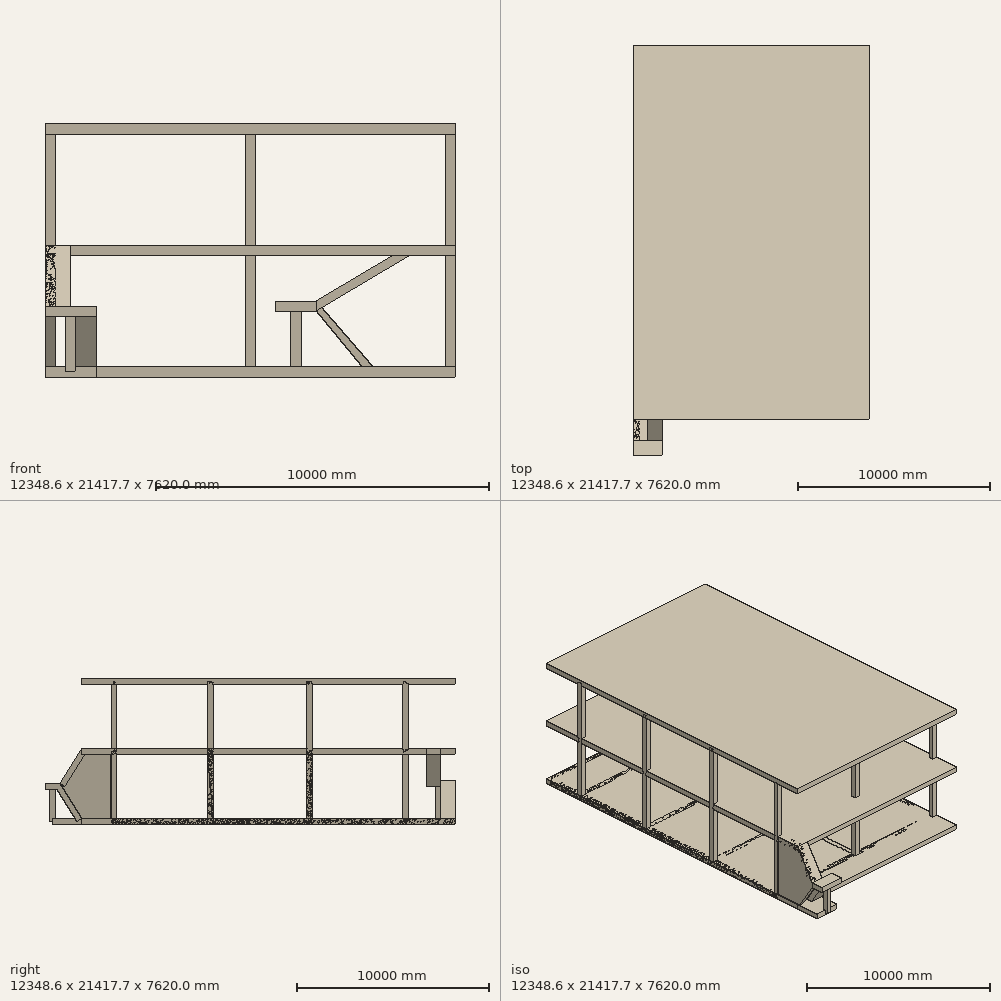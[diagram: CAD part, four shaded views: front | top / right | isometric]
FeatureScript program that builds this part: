
annotation { "Feature Type Name" : "Feature", "Feature Type Description" : "" }
export const myFeature = defineFeature(function(context is Context, id is Id, definition is map)
    precondition{}
    {
        {
            var Q0;
            Q0=qCreatedBy(makeId("Top.planeOp"),FACE);
            var sketch = newSketch(context, id + "F0", { "sketchPlane" : qUnion([Q0])});
            skLineSegment(sketch, "E0.bottom", {"start": v(6172.2, 8991.6) * mm, "end": v(-6172.2, 8991.6) * mm});
            skLineSegment(sketch, "E0.top", {"start": v(6172.2, -8991.6) * mm, "end": v(-6172.2, -8991.6) * mm});
            skLineSegment(sketch, "E0.left", {"start": v(6172.2, 8991.6) * mm, "end": v(6172.2, -8991.6) * mm});
            skLineSegment(sketch, "E0.right", {"start": v(-6172.2, 8991.6) * mm, "end": v(-6172.2, -8991.6) * mm});
            skPoint(sketch, "E0.middle", {"position": v(0, 0) * mm});
            skSolve(sketch);
        }
        {
            var Q0;
            Q0=qCreatedBy(makeId("Top.planeOp"),FACE);
            var sketch = newSketch(context, id + "F1", { "sketchPlane" : qUnion([Q0])});
            skLineSegment(sketch, "E1.bottom", {"start": v(-6172.2, -8991.6) * mm, "end": v(-5867.4, -8991.6) * mm});
            skLineSegment(sketch, "E1.top", {"start": v(-6172.2, -8686.8) * mm, "end": v(-5867.4, -8686.8) * mm});
            skLineSegment(sketch, "E1.left", {"start": v(-6172.2, -8991.6) * mm, "end": v(-6172.2, -8686.8) * mm});
            skLineSegment(sketch, "E1.right", {"start": v(-5867.4, -8991.6) * mm, "end": v(-5867.4, -8686.8) * mm});
            skSolve(sketch);
        }
        {
            var Q0;
            Q0 = qSketchRegion(id + "F1", true);
            extrude(context, id + "F2", {"entities" : qUnion([Q0]), "depth" : 7315.2 * mm, "offsetDistance" : 25.4 * mm});
        }
        {
            var Q0;
            Q0=qCreatedBy(makeId("Top.planeOp"),FACE);
            var sketch = newSketch(context, id + "F3", { "sketchPlane" : qUnion([Q0])});
            skLineSegment(sketch, "E2.bottom", {"start": v(6172.2, -8991.6) * mm, "end": v(5867.4, -8991.6) * mm});
            skLineSegment(sketch, "E2.top", {"start": v(6172.2, -8686.8) * mm, "end": v(5867.4, -8686.8) * mm});
            skLineSegment(sketch, "E2.left", {"start": v(6172.2, -8991.6) * mm, "end": v(6172.2, -8686.8) * mm});
            skLineSegment(sketch, "E2.right", {"start": v(5867.4, -8991.6) * mm, "end": v(5867.4, -8686.8) * mm});
            skSolve(sketch);
        }
        {
            var Q0;
            Q0 = qSketchRegion(id + "F3", true);
            extrude(context, id + "F4", {"entities" : qUnion([Q0]), "depth" : 7315.2 * mm, "offsetDistance" : 25.4 * mm});
        }
        {
            var Q0;
            Q0=qCreatedBy(makeId("Top.planeOp"),FACE);
            var sketch = newSketch(context, id + "F5", { "sketchPlane" : qUnion([Q0])});
            skLineSegment(sketch, "E3.bottom", {"start": v(6172.2, 6553.2) * mm, "end": v(5867.4, 6553.2) * mm});
            skLineSegment(sketch, "E3.top", {"start": v(6172.2, 6248.4) * mm, "end": v(5867.4, 6248.4) * mm});
            skLineSegment(sketch, "E3.left", {"start": v(6172.2, 6553.2) * mm, "end": v(6172.2, 6248.4) * mm});
            skLineSegment(sketch, "E3.right", {"start": v(5867.4, 6553.2) * mm, "end": v(5867.4, 6248.4) * mm});
            skSolve(sketch);
        }
        {
            var Q0;
            Q0 = qSketchRegion(id + "F5", true);
            extrude(context, id + "F6", {"entities" : qUnion([Q0]), "depth" : 7315.2 * mm, "offsetDistance" : 25.4 * mm});
        }
        {
            var Q0;
            Q0=qCreatedBy(makeId("Top.planeOp"),FACE);
            var sketch = newSketch(context, id + "F7", { "sketchPlane" : qUnion([Q0])});
            skLineSegment(sketch, "E4.bottom", {"start": v(-6172.2, 6248.4) * mm, "end": v(-5867.4, 6248.4) * mm});
            skLineSegment(sketch, "E4.top", {"start": v(-6172.2, 6553.2) * mm, "end": v(-5867.4, 6553.2) * mm});
            skLineSegment(sketch, "E4.left", {"start": v(-6172.2, 6248.4) * mm, "end": v(-6172.2, 6553.2) * mm});
            skLineSegment(sketch, "E4.right", {"start": v(-5867.4, 6248.4) * mm, "end": v(-5867.4, 6553.2) * mm});
            skSolve(sketch);
        }
        {
            var Q0;
            Q0 = qSketchRegion(id + "F7", true);
            extrude(context, id + "F8", {"entities" : qUnion([Q0]), "depth" : 7315.2 * mm, "offsetDistance" : 25.4 * mm});
        }
        {
            var Q0;
            Q0=qCreatedBy(makeId("Top.planeOp"),FACE);
            var sketch = newSketch(context, id + "F9", { "sketchPlane" : qUnion([Q0])});
            skLineSegment(sketch, "E5", {"start": v(0, 0) * mm, "end": v(0, 10809.08) * mm});
            skSolve(sketch);
        }
        {
            var Q0;
            Q0=qCreatedBy(makeId("Top.planeOp"),FACE);
            var sketch = newSketch(context, id + "F10", { "sketchPlane" : qUnion([Q0])});
            skLineSegment(sketch, "E6.bottom", {"start": v(152.4, 6248.4) * mm, "end": v(-152.4, 6248.4) * mm});
            skLineSegment(sketch, "E6.top", {"start": v(152.4, 6553.2) * mm, "end": v(-152.4, 6553.2) * mm});
            skLineSegment(sketch, "E6.left", {"start": v(152.4, 6248.4) * mm, "end": v(152.4, 6553.2) * mm});
            skLineSegment(sketch, "E6.right", {"start": v(-152.4, 6248.4) * mm, "end": v(-152.4, 6553.2) * mm});
            skPoint(sketch, "E6.middle", {"position": v(0, 6400.8) * mm});
            skSolve(sketch);
        }
        {
            var Q0;
            Q0=makeQuery(id+"F10.imprint","IMPRINT",FACE,{"disambiguationData":[TD([[makeQuery(id+"F10.imprint","IMPRINT",EDGE,{"derivedFrom":sQuery(id+"F10.wireOp",EDGE,"E6.bottom")}),-1.0]])]});
            extrude(context, id + "F11", {"entities" : qUnion([Q0]), "depth" : 7315.2 * mm, "offsetDistance" : 25.4 * mm});
        }
        {
            var Q0;
            Q0=qCreatedBy(makeId("Top.planeOp"),FACE);
            var sketch = newSketch(context, id + "F12", { "sketchPlane" : qUnion([Q0])});
            skLineSegment(sketch, "E7.bottom", {"start": v(152.4, -8991.6) * mm, "end": v(-152.4, -8991.6) * mm});
            skLineSegment(sketch, "E7.top", {"start": v(152.4, -8686.8) * mm, "end": v(-152.4, -8686.8) * mm});
            skLineSegment(sketch, "E7.left", {"start": v(152.4, -8991.6) * mm, "end": v(152.4, -8686.8) * mm});
            skLineSegment(sketch, "E7.right", {"start": v(-152.4, -8991.6) * mm, "end": v(-152.4, -8686.8) * mm});
            skPoint(sketch, "E7.middle", {"position": v(0, -8839.2) * mm});
            skSolve(sketch);
        }
        {
            var Q0;
            Q0 = qSketchRegion(id + "F12", true);
            extrude(context, id + "F13", {"entities" : qUnion([Q0]), "depth" : 7315.2 * mm, "offsetDistance" : 25.4 * mm});
        }
        {
            var Q0;
            Q0=qCreatedBy(makeId("Top.planeOp"),FACE);
            var sketch = newSketch(context, id + "F14", { "sketchPlane" : qUnion([Q0])});
            skLineSegment(sketch, "E8.bottom", {"start": v(152.4, -3962.4) * mm, "end": v(-152.4, -3962.4) * mm});
            skLineSegment(sketch, "E8.top", {"start": v(152.4, -3657.6) * mm, "end": v(-152.4, -3657.6) * mm});
            skLineSegment(sketch, "E8.left", {"start": v(152.4, -3962.4) * mm, "end": v(152.4, -3657.6) * mm});
            skLineSegment(sketch, "E8.right", {"start": v(-152.4, -3962.4) * mm, "end": v(-152.4, -3657.6) * mm});
            skPoint(sketch, "E8.middle", {"position": v(0, -3810) * mm});
            skSolve(sketch);
        }
        {
            var Q0;
            Q0=qCreatedBy(makeId("Top.planeOp"),FACE);
            var sketch = newSketch(context, id + "F15", { "sketchPlane" : qUnion([Q0])});
            skLineSegment(sketch, "E9.bottom", {"start": v(152.4, 1219.2) * mm, "end": v(-152.4, 1219.2) * mm});
            skLineSegment(sketch, "E9.top", {"start": v(152.4, 1524) * mm, "end": v(-152.4, 1524) * mm});
            skLineSegment(sketch, "E9.left", {"start": v(152.4, 1219.2) * mm, "end": v(152.4, 1524) * mm});
            skLineSegment(sketch, "E9.right", {"start": v(-152.4, 1219.2) * mm, "end": v(-152.4, 1524) * mm});
            skPoint(sketch, "E9.middle", {"position": v(0, 1371.6) * mm});
            skSolve(sketch);
        }
        {
            var Q0;
            Q0=makeQuery(id+"F14.imprint","IMPRINT",FACE,{"disambiguationData":[TD([[makeQuery(id+"F14.imprint","IMPRINT",EDGE,{"derivedFrom":sQuery(id+"F14.wireOp",EDGE,"E8.bottom")}),-1.0]])]});
            extrude(context, id + "F16", {"entities" : qUnion([Q0]), "depth" : 7315.2 * mm, "offsetDistance" : 25.4 * mm});
        }
        {
            var Q0;
            Q0 = qSketchRegion(id + "F15", true);
            extrude(context, id + "F17", {"entities" : qUnion([Q0]), "depth" : 7315.2 * mm, "offsetDistance" : 25.4 * mm});
        }
        {
            var Q0;
            Q0=qCreatedBy(makeId("Top.planeOp"),FACE);
            var sketch = newSketch(context, id + "F18", { "sketchPlane" : qUnion([Q0])});
            skLineSegment(sketch, "E10.bottom", {"start": v(6172.2, 1219.2) * mm, "end": v(5867.4, 1219.2) * mm});
            skLineSegment(sketch, "E10.top", {"start": v(6172.2, 1524) * mm, "end": v(5867.4, 1524) * mm});
            skLineSegment(sketch, "E10.left", {"start": v(6172.2, 1219.2) * mm, "end": v(6172.2, 1524) * mm});
            skLineSegment(sketch, "E10.right", {"start": v(5867.4, 1219.2) * mm, "end": v(5867.4, 1524) * mm});
            skPoint(sketch, "E10.middle", {"position": v(6019.8, 1371.6) * mm});
            skLineSegment(sketch, "E11.bottom", {"start": v(-5867.4, 1219.2) * mm, "end": v(-6172.2, 1219.2) * mm});
            skLineSegment(sketch, "E11.top", {"start": v(-5867.4, 1524) * mm, "end": v(-6172.2, 1524) * mm});
            skLineSegment(sketch, "E11.left", {"start": v(-5867.4, 1219.2) * mm, "end": v(-5867.4, 1524) * mm});
            skLineSegment(sketch, "E11.right", {"start": v(-6172.2, 1219.2) * mm, "end": v(-6172.2, 1524) * mm});
            skPoint(sketch, "E11.middle", {"position": v(-6019.8, 1371.6) * mm});
            skLineSegment(sketch, "E12.bottom", {"start": v(-5867.4, -3962.4) * mm, "end": v(-6172.2, -3962.4) * mm});
            skLineSegment(sketch, "E12.top", {"start": v(-5867.4, -3657.6) * mm, "end": v(-6172.2, -3657.6) * mm});
            skLineSegment(sketch, "E12.left", {"start": v(-5867.4, -3962.4) * mm, "end": v(-5867.4, -3657.6) * mm});
            skLineSegment(sketch, "E12.right", {"start": v(-6172.2, -3962.4) * mm, "end": v(-6172.2, -3657.6) * mm});
            skPoint(sketch, "E12.middle", {"position": v(-6019.8, -3810) * mm});
            skLineSegment(sketch, "E13.bottom", {"start": v(6172.2, -3962.4) * mm, "end": v(5867.4, -3962.4) * mm});
            skLineSegment(sketch, "E13.top", {"start": v(6172.2, -3657.6) * mm, "end": v(5867.4, -3657.6) * mm});
            skLineSegment(sketch, "E13.left", {"start": v(6172.2, -3962.4) * mm, "end": v(6172.2, -3657.6) * mm});
            skLineSegment(sketch, "E13.right", {"start": v(5867.4, -3962.4) * mm, "end": v(5867.4, -3657.6) * mm});
            skPoint(sketch, "E13.middle", {"position": v(6019.8, -3810) * mm});
            skSolve(sketch);
        }
        {
            var Q0;
            Q0=makeQuery(id+"F18.imprint","IMPRINT",FACE,{"disambiguationData":[TD([[makeQuery(id+"F18.imprint","IMPRINT",EDGE,{"derivedFrom":sQuery(id+"F18.wireOp",EDGE,"E13.bottom")}),-1.0]])]});
            extrude(context, id + "F19", {"entities" : qUnion([Q0]), "depth" : 3657.6 * mm, "offsetDistance" : 25.4 * mm});
        }
        {
            var Q0;
            Q0=makeQuery(id+"F18.imprint","IMPRINT",FACE,{"disambiguationData":[TD([[makeQuery(id+"F18.imprint","IMPRINT",EDGE,{"derivedFrom":sQuery(id+"F18.wireOp",EDGE,"E10.bottom")}),-1.0]])]});
            extrude(context, id + "F20", {"entities" : qUnion([Q0]), "depth" : 3657.6 * mm, "offsetDistance" : 25.4 * mm});
        }
        {
            var Q0;
            Q0 = qSketchRegion(id + "F18", true);
            extrude(context, id + "F21", {"entities" : qUnion([Q0]), "depth" : 7315.2 * mm, "offsetDistance" : 25.4 * mm});
        }
        {
            var Q0;
            Q0=qCreatedBy(makeId("Top.planeOp"),FACE);
            var sketch = newSketch(context, id + "F22", { "sketchPlane" : qUnion([Q0])});
            skLineSegment(sketch, "E14.bottom", {"start": v(6172.2, 6248.4) * mm, "end": v(-6172.2, 6248.4) * mm});
            skLineSegment(sketch, "E14.top", {"start": v(6172.2, 6553.2) * mm, "end": v(-6172.2, 6553.2) * mm});
            skLineSegment(sketch, "E14.left", {"start": v(6172.2, 6248.4) * mm, "end": v(6172.2, 6553.2) * mm});
            skLineSegment(sketch, "E14.right", {"start": v(-6172.2, 6248.4) * mm, "end": v(-6172.2, 6553.2) * mm});
            skPoint(sketch, "E14.middle", {"position": v(0, 6400.8) * mm});
            skSolve(sketch);
        }
        {
            var Q0;
            Q0=qCreatedBy(makeId("Top.planeOp"),FACE);
            var sketch = newSketch(context, id + "F23", { "sketchPlane" : qUnion([Q0])});
            skLineSegment(sketch, "E15.bottom", {"start": v(6172.2, 1219.2) * mm, "end": v(-6172.2, 1219.2) * mm});
            skLineSegment(sketch, "E15.top", {"start": v(6172.2, 1524) * mm, "end": v(-6172.2, 1524) * mm});
            skLineSegment(sketch, "E15.left", {"start": v(6172.2, 1219.2) * mm, "end": v(6172.2, 1524) * mm});
            skLineSegment(sketch, "E15.right", {"start": v(-6172.2, 1219.2) * mm, "end": v(-6172.2, 1524) * mm});
            skPoint(sketch, "E15.middle", {"position": v(0, 1371.6) * mm});
            skSolve(sketch);
        }
        {
            var Q0;
            Q0=qCreatedBy(makeId("Top.planeOp"),FACE);
            var sketch = newSketch(context, id + "F24", { "sketchPlane" : qUnion([Q0])});
            skLineSegment(sketch, "E16.bottom", {"start": v(6172.2, -3962.4) * mm, "end": v(-6172.2, -3962.4) * mm});
            skLineSegment(sketch, "E16.top", {"start": v(6172.2, -3657.6) * mm, "end": v(-6172.2, -3657.6) * mm});
            skLineSegment(sketch, "E16.left", {"start": v(6172.2, -3962.4) * mm, "end": v(6172.2, -3657.6) * mm});
            skLineSegment(sketch, "E16.right", {"start": v(-6172.2, -3962.4) * mm, "end": v(-6172.2, -3657.6) * mm});
            skPoint(sketch, "E16.middle", {"position": v(0, -3810) * mm});
            skSolve(sketch);
        }
        {
            var Q0;
            Q0=qCreatedBy(makeId("Top.planeOp"),FACE);
            var sketch = newSketch(context, id + "F25", { "sketchPlane" : qUnion([Q0])});
            skLineSegment(sketch, "E17.bottom", {"start": v(6172.2, -8991.6) * mm, "end": v(-6172.2, -8991.6) * mm});
            skLineSegment(sketch, "E17.top", {"start": v(6172.2, -8686.8) * mm, "end": v(-6172.2, -8686.8) * mm});
            skLineSegment(sketch, "E17.left", {"start": v(6172.2, -8991.6) * mm, "end": v(6172.2, -8686.8) * mm});
            skLineSegment(sketch, "E17.right", {"start": v(-6172.2, -8991.6) * mm, "end": v(-6172.2, -8686.8) * mm});
            skPoint(sketch, "E17.middle", {"position": v(0, -8839.2) * mm});
            skSolve(sketch);
        }
        {
            var Q0;
            Q0 = qSketchRegion(id + "F25", true);
            extrude(context, id + "F26", {"entities" : qUnion([Q0]), "endBound" : BoundingType.SYMMETRIC, "depth" : 304.8 * mm, "offsetDistance" : 25.4 * mm});
        }
        {
            var Q0;
            Q0 = qSketchRegion(id + "F24", true);
            var Q1;
            Q1 = qSketchRegion(id + "F23", true);
            extrude(context, id + "F27", {"entities" : qUnion([Q0, Q1]), "endBound" : BoundingType.SYMMETRIC, "depth" : 304.8 * mm, "offsetDistance" : 25.4 * mm});
        }
        {
            var Q0;
            Q0 = qSketchRegion(id + "F22", true);
            extrude(context, id + "F28", {"entities" : qUnion([Q0]), "endBound" : BoundingType.SYMMETRIC, "depth" : 304.8 * mm, "offsetDistance" : 25.4 * mm});
        }
        {
            var Q0;
            Q0=qCreatedBy(makeId("Top.planeOp"),FACE);
            var sketch = newSketch(context, id + "F29", { "sketchPlane" : qUnion([Q0])});
            skLineSegment(sketch, "E18.bottom", {"start": v(152.4, 8991.6) * mm, "end": v(-152.4, 8991.6) * mm});
            skLineSegment(sketch, "E18.top", {"start": v(152.4, -8991.6) * mm, "end": v(-152.4, -8991.6) * mm});
            skLineSegment(sketch, "E18.left", {"start": v(152.4, 8991.6) * mm, "end": v(152.4, -8991.6) * mm});
            skLineSegment(sketch, "E18.right", {"start": v(-152.4, 8991.6) * mm, "end": v(-152.4, -8991.6) * mm});
            skPoint(sketch, "E18.middle", {"position": v(0, 0) * mm});
            skSolve(sketch);
        }
        {
            var Q0;
            Q0=qCreatedBy(makeId("Top.planeOp"),FACE);
            var sketch = newSketch(context, id + "F30", { "sketchPlane" : qUnion([Q0])});
            skLineSegment(sketch, "E19.bottom", {"start": v(6172.2, 8991.6) * mm, "end": v(5867.4, 8991.6) * mm});
            skLineSegment(sketch, "E19.top", {"start": v(6172.2, -8991.6) * mm, "end": v(5867.4, -8991.6) * mm});
            skLineSegment(sketch, "E19.left", {"start": v(6172.2, 8991.6) * mm, "end": v(6172.2, -8991.6) * mm});
            skLineSegment(sketch, "E19.right", {"start": v(5867.4, 8991.6) * mm, "end": v(5867.4, -8991.6) * mm});
            skPoint(sketch, "E19.middle", {"position": v(6019.8, 0) * mm});
            skSolve(sketch);
        }
        {
            var Q0;
            Q0=qCreatedBy(makeId("Top.planeOp"),FACE);
            var sketch = newSketch(context, id + "F31", { "sketchPlane" : qUnion([Q0])});
            skLineSegment(sketch, "E20.bottom", {"start": v(-5867.4, 8991.6) * mm, "end": v(-6172.2, 8991.6) * mm});
            skLineSegment(sketch, "E20.top", {"start": v(-5867.4, -8991.6) * mm, "end": v(-6172.2, -8991.6) * mm});
            skLineSegment(sketch, "E20.left", {"start": v(-5867.4, 8991.6) * mm, "end": v(-5867.4, -8991.6) * mm});
            skLineSegment(sketch, "E20.right", {"start": v(-6172.2, 8991.6) * mm, "end": v(-6172.2, -8991.6) * mm});
            skPoint(sketch, "E20.middle", {"position": v(-6019.8, 0) * mm});
            skSolve(sketch);
        }
        {
            var Q0;
            Q0 = qSketchRegion(id + "F31", true);
            var Q1;
            Q1 = qSketchRegion(id + "F30", true);
            var Q2;
            Q2 = qSketchRegion(id + "F29", true);
            extrude(context, id + "F32", {"entities" : qUnion([Q0, Q1, Q2]), "endBound" : BoundingType.SYMMETRIC, "depth" : 304.8 * mm, "offsetDistance" : 25.4 * mm});
        }
        {
            var Q0;
            Q0=qCreatedBy(makeId("Top.planeOp"),FACE);
            var sketch = newSketch(context, id + "F33", { "sketchPlane" : qUnion([Q0])});
            skLineSegment(sketch, "E21.bottom", {"start": v(6172.2, 8686.8) * mm, "end": v(-6172.2, 8686.8) * mm});
            skLineSegment(sketch, "E21.top", {"start": v(6172.2, 8991.6) * mm, "end": v(-6172.2, 8991.6) * mm});
            skLineSegment(sketch, "E21.left", {"start": v(6172.2, 8686.8) * mm, "end": v(6172.2, 8991.6) * mm});
            skLineSegment(sketch, "E21.right", {"start": v(-6172.2, 8686.8) * mm, "end": v(-6172.2, 8991.6) * mm});
            skPoint(sketch, "E21.middle", {"position": v(0, 8839.2) * mm});
            skSolve(sketch);
        }
        {
            var Q0;
            Q0 = qSketchRegion(id + "F33", true);
            extrude(context, id + "F34", {"entities" : qUnion([Q0]), "endBound" : BoundingType.SYMMETRIC, "depth" : 304.8 * mm, "offsetDistance" : 25.4 * mm});
        }
        {
            var Q0;
            Q0=qCreatedBy(makeId("Top.planeOp"),FACE);
            var sketch = newSketch(context, id + "F35", { "sketchPlane" : qUnion([Q0])});
            skLineSegment(sketch, "E22.bottom", {"start": v(-6172.2, 8991.6) * mm, "end": v(6172.2, 8991.6) * mm});
            skLineSegment(sketch, "E22.top", {"start": v(-6172.2, -10515.6) * mm, "end": v(6172.2, -10515.6) * mm});
            skLineSegment(sketch, "E22.left", {"start": v(-6172.2, 8991.6) * mm, "end": v(-6172.2, -10515.6) * mm});
            skLineSegment(sketch, "E22.right", {"start": v(6172.2, 8991.6) * mm, "end": v(6172.2, -10515.6) * mm});
            skSolve(sketch);
        }
        {
            var Q0;
            Q0=qCreatedBy(makeId("Top.planeOp"),FACE);
            cPlane(context, id + "F36", {"entities" : qUnion([Q0]), "cplaneType" : CPlaneType.OFFSET, "offset" : 3657.6 * mm, "width" : 152.4 * mm, "height" : 152.4 * mm});
        }
        {
            var Q0;
            Q0=qCreatedBy(id+"F36.planeOp",FACE);
            var sketch = newSketch(context, id + "F37", { "sketchPlane" : qUnion([Q0])});
            skLineSegment(sketch, "E23.bottom", {"start": v(-6172.2, 8991.6) * mm, "end": v(6172.2, 8991.6) * mm});
            skLineSegment(sketch, "E23.top", {"start": v(-6172.2, -10515.6) * mm, "end": v(6172.2, -10515.6) * mm});
            skLineSegment(sketch, "E23.left", {"start": v(-6172.2, 8991.6) * mm, "end": v(-6172.2, -10515.6) * mm});
            skLineSegment(sketch, "E23.right", {"start": v(6172.2, 8991.6) * mm, "end": v(6172.2, -10515.6) * mm});
            skSolve(sketch);
        }
        {
            var Q0;
            Q0 = qSketchRegion(id + "F35", true);
            var Q1;
            Q1 = qSketchRegion(id + "F37", true);
            extrude(context, id + "F38", {"entities" : qUnion([Q0, Q1]), "endBound" : BoundingType.SYMMETRIC, "depth" : 304.8 * mm, "offsetDistance" : 25.4 * mm});
        }
        {
            var Q0;
            Q0=qCreatedBy(id+"F36.planeOp",FACE);
            cPlane(context, id + "F39", {"entities" : qUnion([Q0]), "cplaneType" : CPlaneType.OFFSET, "offset" : 3657.6 * mm, "width" : 152.4 * mm, "height" : 152.4 * mm});
        }
        {
            var Q0;
            Q0=qCreatedBy(id+"F39.planeOp",FACE);
            var sketch = newSketch(context, id + "F40", { "sketchPlane" : qUnion([Q0])});
            skLineSegment(sketch, "E24.bottom", {"start": v(-6172.2, 8991.6) * mm, "end": v(6172.2, 8991.6) * mm});
            skLineSegment(sketch, "E24.top", {"start": v(-6172.2, -10515.6) * mm, "end": v(6172.2, -10515.6) * mm});
            skLineSegment(sketch, "E24.left", {"start": v(-6172.2, 8991.6) * mm, "end": v(-6172.2, -10515.6) * mm});
            skLineSegment(sketch, "E24.right", {"start": v(6172.2, 8991.6) * mm, "end": v(6172.2, -10515.6) * mm});
            skSolve(sketch);
        }
        {
            var Q0;
            Q0 = qSketchRegion(id + "F40", true);
            var Q1;
            Q1=sQuery(id+"F40.wireOp",EDGE,"E24.bottom");
            var Q2;
            Q2=sQuery(id+"F40.wireOp",EDGE,"E24.top");
            var Q3;
            Q3=sQuery(id+"F40.wireOp",EDGE,"E24.left");
            var Q4;
            Q4=sQuery(id+"F40.wireOp",EDGE,"E24.right");
            extrude(context, id + "F41", {"entities" : qUnion([Q0]), "surfaceEntities" : qUnion([Q1, Q2, Q3, Q4]), "endBound" : BoundingType.SYMMETRIC, "depth" : 304.8 * mm, "offsetDistance" : 25.4 * mm});
        }
        {
            var Q0;
            Q0=qCreatedBy(makeId("Top.planeOp"),FACE);
            cPlane(context, id + "F42", {"entities" : qUnion([Q0]), "cplaneType" : CPlaneType.OFFSET, "offset" : 1828.8 * mm, "width" : 152.4 * mm, "height" : 152.4 * mm});
        }
        {
            var Q0;
            Q0=qCreatedBy(id+"F42.planeOp",FACE);
            var sketch = newSketch(context, id + "F43", { "sketchPlane" : qUnion([Q0])});
            skLineSegment(sketch, "E25.bottom", {"start": v(-6172.2, -11658.6) * mm, "end": v(-4648.2, -11658.6) * mm});
            skLineSegment(sketch, "E25.top", {"start": v(-6172.2, -12420.6) * mm, "end": v(-4648.2, -12420.6) * mm});
            skLineSegment(sketch, "E25.left", {"start": v(-6172.2, -11658.6) * mm, "end": v(-6172.2, -12420.6) * mm});
            skLineSegment(sketch, "E25.right", {"start": v(-4648.2, -11658.6) * mm, "end": v(-4648.2, -12420.6) * mm});
            skLineSegment(sketch, "E26.bottom", {"start": v(-5562.6, -11887.2) * mm, "end": v(-5257.8, -11887.2) * mm});
            skLineSegment(sketch, "E26.top", {"start": v(-5562.6, -12192) * mm, "end": v(-5257.8, -12192) * mm});
            skLineSegment(sketch, "E26.left", {"start": v(-5562.6, -11887.2) * mm, "end": v(-5562.6, -12192) * mm});
            skLineSegment(sketch, "E26.right", {"start": v(-5257.8, -11887.2) * mm, "end": v(-5257.8, -12192) * mm});
            skSolve(sketch);
        }
        {
            var Q0;
            Q0=makeQuery(id+"F43.imprint","IMPRINT",FACE,{"disambiguationData":[TD([[makeQuery(id+"F43.imprint","IMPRINT",EDGE,{"derivedFrom":sQuery(id+"F43.wireOp",EDGE,"E26.bottom")}),-1.0]])]});
            extrude(context, id + "F44", {"entities" : qUnion([Q0]), "oppositeDirection" : true, "depth" : 1828.8 * mm, "offsetDistance" : 25.4 * mm});
        }
        {
            var Q0;
            Q0 = qSketchRegion(id + "F43", true);
            var Q1;
            Q1=makeQuery(id+"F44.opExtrude","CAP_FACE",FACE,{"disambiguationData":[OSD([sQuery(id+"F43.wireOp",EDGE,"E26.bottom"),sQuery(id+"F43.wireOp",EDGE,"E26.top"),sQuery(id+"F43.wireOp",EDGE,"E26.left"),sQuery(id+"F43.wireOp",EDGE,"E26.right")])],"isStart":true});
            extrude(context, id + "F45", {"entities" : qUnion([Q0, Q1]), "endBound" : BoundingType.SYMMETRIC, "depth" : 304.8 * mm, "offsetDistance" : 25.4 * mm});
        }
        {
            var Q0;
            Q0=makeQuery(id+"F45.opExtrude","CAP_VERTEX",VERTEX,{"disambiguationData":[OSD([sQuery(id+"F43.wireOp",EDGE,"E25.bottom"),sQuery(id+"F43.wireOp",EDGE,"E25.left")])],"isStart":false});
            var Q1;
            Q1=makeQuery(id+"F45.opExtrude","CAP_VERTEX",VERTEX,{"disambiguationData":[OSD([sQuery(id+"F43.wireOp",EDGE,"E25.bottom"),sQuery(id+"F43.wireOp",EDGE,"E25.right")])],"isStart":false});
            var Q2;
            Q2=makeQuery(id+"F38.opExtrude","CAP_VERTEX",VERTEX,{"disambiguationData":[OSD([sQuery(id+"F37.wireOp",EDGE,"E23.top"),sQuery(id+"F37.wireOp",EDGE,"E23.left")])],"isStart":false});
            cPlane(context, id + "F46", {"entities" : qUnion([Q0, Q1, Q2]), "cplaneType" : CPlaneType.THREE_POINT, "offset" : 25.4 * mm, "width" : 152.4 * mm, "height" : 152.4 * mm});
        }
        {
            var Q0;
            Q0=qCreatedBy(id+"F46.planeOp",FACE);
            var sketch = newSketch(context, id + "F47", { "sketchPlane" : qUnion([Q0])});
            skLineSegment(sketch, "E27.bottom", {"start": v(6172.2, -2342.38) * mm, "end": v(6172.2, -2342.38) * mm});
            skLineSegment(sketch, "E27.top", {"start": v(6172.2, -4499) * mm, "end": v(6172.2, -4499) * mm});
            skLineSegment(sketch, "E28.bottom", {"start": v(6172.2, -2342.38) * mm, "end": v(5410.2, -2342.38) * mm});
            skLineSegment(sketch, "E28.top", {"start": v(6172.2, -4499) * mm, "end": v(5410.2, -4499) * mm});
            skLineSegment(sketch, "E28.left", {"start": v(6172.2, -2342.38) * mm, "end": v(6172.2, -4499) * mm});
            skLineSegment(sketch, "E28.right", {"start": v(5410.2, -2342.38) * mm, "end": v(5410.2, -4499) * mm});
            skSolve(sketch);
        }
        {
            var Q0;
            Q0 = qSketchRegion(id + "F47", true);
            extrude(context, id + "F48", {"entities" : qUnion([Q0]), "operationType" : NewBodyOperationType.ADD, "depth" : 304.8 * mm, "offsetDistance" : 25.4 * mm});
        }
        {
            var Q0;
            Q0=makeQuery(id+"F45.opExtrude","CAP_VERTEX",VERTEX,{"disambiguationData":[OSD([sQuery(id+"F43.wireOp",EDGE,"E25.bottom"),sQuery(id+"F43.wireOp",EDGE,"E25.right")])],"isStart":false});
            var Q1;
            Q1=makeQuery(id+"F38.opExtrude","CAP_VERTEX",VERTEX,{"disambiguationData":[OSD([sQuery(id+"F35.wireOp",EDGE,"E22.top"),sQuery(id+"F35.wireOp",EDGE,"E22.left")])],"isStart":false});
            var Q2;
            Q2=makeQuery(id+"F38.opExtrude","CAP_VERTEX",VERTEX,{"disambiguationData":[OSD([sQuery(id+"F35.wireOp",EDGE,"E22.top"),sQuery(id+"F35.wireOp",EDGE,"E22.right")])],"isStart":false});
            cPlane(context, id + "F49", {"entities" : qUnion([Q0, Q1, Q2]), "cplaneType" : CPlaneType.THREE_POINT, "offset" : 25.4 * mm, "width" : 152.4 * mm, "height" : 152.4 * mm});
        }
        {
            var Q0;
            Q0=qCreatedBy(id+"F49.planeOp",FACE);
            var sketch = newSketch(context, id + "F50", { "sketchPlane" : qUnion([Q0])});
            skLineSegment(sketch, "E29.bottom", {"start": v(5410.2, 7859.1) * mm, "end": v(4648.2, 7859.1) * mm});
            skLineSegment(sketch, "E29.top", {"start": v(5410.2, 5702.5) * mm, "end": v(4648.2, 5702.5) * mm});
            skLineSegment(sketch, "E29.left", {"start": v(5410.2, 7859.1) * mm, "end": v(5410.2, 5702.5) * mm});
            skLineSegment(sketch, "E29.right", {"start": v(4648.2, 7859.1) * mm, "end": v(4648.2, 5702.5) * mm});
            skSolve(sketch);
        }
        {
            var Q0;
            Q0 = qSketchRegion(id + "F50", true);
            extrude(context, id + "F51", {"entities" : qUnion([Q0]), "operationType" : NewBodyOperationType.ADD, "oppositeDirection" : true, "depth" : 304.8 * mm, "offsetDistance" : 25.4 * mm});
        }
        {
            var Q0;
            Q0=makeQuery(id+"F38.opExtrude","SWEPT_FACE",FACE,{"disambiguationData":[OSD([sQuery(id+"F35.wireOp",EDGE,"E22.top")])]});
            var sketch = newSketch(context, id + "F52", { "sketchPlane" : qUnion([Q0])});
            skLineSegment(sketch, "E30.bottom", {"start": v(-6172.2, 152.4) * mm, "end": v(-4648.2, 152.4) * mm});
            skLineSegment(sketch, "E30.top", {"start": v(-6172.2, -152.4) * mm, "end": v(-4648.2, -152.4) * mm});
            skLineSegment(sketch, "E30.left", {"start": v(-6172.2, 152.4) * mm, "end": v(-6172.2, -152.4) * mm});
            skLineSegment(sketch, "E30.right", {"start": v(-4648.2, 152.4) * mm, "end": v(-4648.2, -152.4) * mm});
            skSolve(sketch);
        }
        {
            var Q0;
            Q0 = qSketchRegion(id + "F52", true);
            extrude(context, id + "F53", {"entities" : qUnion([Q0]), "depth" : 1524 * mm, "offsetDistance" : 25.4 * mm});
        }
        {
            var Q0;
            Q0=makeQuery(id+"F48.boolean.opBoolean","MERGE",FACE,{"derivedFrom":[makeQuery(id+"F38.opExtrude","SWEPT_FACE",FACE,{"disambiguationData":[OSD([sQuery(id+"F37.wireOp",EDGE,"E23.left")])]}),makeQuery(id+"F48.opExtrude","SWEPT_FACE",FACE,{"disambiguationData":[OSD([sQuery(id+"F47.wireOp",EDGE,"E28.left")])]})]});
            var sketch = newSketch(context, id + "F54", { "sketchPlane" : qUnion([Q0])});
            skLineSegment(sketch, "E31", {"start": v(9003.77, 3505.2) * mm, "end": v(9003.77, 159.3) * mm});
            skLineSegment(sketch, "E32", {"start": v(9003.77, 159.3) * mm, "end": v(10679.62, 159.3) * mm});
            skLineSegment(sketch, "E33", {"start": v(10679.62, 159.3) * mm, "end": v(11658.6, 1659.61) * mm});
            skLineSegment(sketch, "E34", {"start": v(11658.6, 1659.61) * mm, "end": v(11658.6, 1981.2) * mm});
            skLineSegment(sketch, "E35", {"start": v(11658.6, 1981.2) * mm, "end": v(10515.6, 3810) * mm});
            skLineSegment(sketch, "E36", {"start": v(10515.6, 3810) * mm, "end": v(9003.77, 3810) * mm});
            skLineSegment(sketch, "E37", {"start": v(9003.77, 3810) * mm, "end": v(9003.77, 3505.2) * mm});
            skSolve(sketch);
        }
        {
            var Q0;
            Q0 = qSketchRegion(id + "F54", true);
            extrude(context, id + "F55", {"entities" : qUnion([Q0]), "oppositeDirection" : true, "depth" : 304.8 * mm, "offsetDistance" : 25.4 * mm});
        }
        {
            var Q0;
            Q0=makeQuery(id+"F38.opExtrude","SWEPT_FACE",FACE,{"disambiguationData":[OSD([sQuery(id+"F37.wireOp",EDGE,"E23.right")])]});
            var sketch = newSketch(context, id + "F56", { "sketchPlane" : qUnion([Q0])});
            skLineSegment(sketch, "E38.bottom", {"start": v(8991.6, 3505.2) * mm, "end": v(7467.6, 3505.2) * mm});
            skLineSegment(sketch, "E38.top", {"start": v(8991.6, 3810) * mm, "end": v(7467.6, 3810) * mm});
            skLineSegment(sketch, "E38.left", {"start": v(8991.6, 3505.2) * mm, "end": v(8991.6, 3810) * mm});
            skLineSegment(sketch, "E38.right", {"start": v(7467.6, 3505.2) * mm, "end": v(7467.6, 3810) * mm});
            skSolve(sketch);
        }
        {
            var Q0;
            Q0 = qSketchRegion(id + "F56", true);
            extrude(context, id + "F57", {"entities" : qUnion([Q0]), "operationType" : NewBodyOperationType.REMOVE, "oppositeDirection" : true, "depth" : 3048 * mm, "offsetDistance" : 25.4 * mm});
        }
        {
            var Q0;
            Q0=makeQuery(id+"F38.opExtrude","CAP_FACE",FACE,{"disambiguationData":[OSD([sQuery(id+"F35.wireOp",EDGE,"E22.bottom"),sQuery(id+"F35.wireOp",EDGE,"E22.top"),sQuery(id+"F35.wireOp",EDGE,"E22.left"),sQuery(id+"F35.wireOp",EDGE,"E22.right")])],"isStart":false});
            var sketch = newSketch(context, id + "F58", { "sketchPlane" : qUnion([Q0])});
            skLineSegment(sketch, "E39.bottom", {"start": v(1219.2, 7930.33) * mm, "end": v(1524, 7930.33) * mm});
            skLineSegment(sketch, "E39.top", {"start": v(1219.2, 8235.13) * mm, "end": v(1524, 8235.13) * mm});
            skLineSegment(sketch, "E39.left", {"start": v(1219.2, 7930.33) * mm, "end": v(1219.2, 8235.13) * mm});
            skLineSegment(sketch, "E39.right", {"start": v(1524, 7930.33) * mm, "end": v(1524, 8235.13) * mm});
            skSolve(sketch);
        }
        {
            var Q0;
            Q0 = qSketchRegion(id + "F58", true);
            extrude(context, id + "F59", {"entities" : qUnion([Q0]), "operationType" : NewBodyOperationType.ADD, "depth" : 1828.8 * mm, "offsetDistance" : 25.4 * mm});
        }
        {
            var Q0;
            Q0=makeQuery(id+"F59.opExtrude","CAP_FACE",FACE,{"disambiguationData":[OSD([sQuery(id+"F58.wireOp",EDGE,"E39.bottom"),sQuery(id+"F58.wireOp",EDGE,"E39.top"),sQuery(id+"F58.wireOp",EDGE,"E39.left"),sQuery(id+"F58.wireOp",EDGE,"E39.right")])],"isStart":false});
            var sketch = newSketch(context, id + "F60", { "sketchPlane" : qUnion([Q0])});
            skLineSegment(sketch, "E40.bottom", {"start": v(762, 7467.6) * mm, "end": v(1981.2, 7467.6) * mm});
            skLineSegment(sketch, "E40.top", {"start": v(762, 8991.6) * mm, "end": v(1981.2, 8991.6) * mm});
            skLineSegment(sketch, "E40.left", {"start": v(762, 7467.6) * mm, "end": v(762, 8991.6) * mm});
            skLineSegment(sketch, "E40.right", {"start": v(1981.2, 7467.6) * mm, "end": v(1981.2, 8991.6) * mm});
            skSolve(sketch);
        }
        {
            var Q0;
            Q0 = qSketchRegion(id + "F60", true);
            extrude(context, id + "F61", {"entities" : qUnion([Q0]), "operationType" : NewBodyOperationType.ADD, "endBound" : BoundingType.SYMMETRIC, "depth" : 304.8 * mm, "offsetDistance" : 25.4 * mm});
        }
        {
            var Q0;
            Q0=makeQuery(id+"F59.opExtrude","SWEPT_FACE",FACE,{"disambiguationData":[OSD([sQuery(id+"F58.wireOp",EDGE,"E39.top")])]});
            var sketch = newSketch(context, id + "F62", { "sketchPlane" : qUnion([Q0])});
            skLineSegment(sketch, "E41", {"start": v(-1981.2, 2133.6) * mm, "end": v(-3697.76, 152.4) * mm});
            skLineSegment(sketch, "E42", {"start": v(-3697.76, 152.4) * mm, "end": v(-3368.67, 152.4) * mm});
            skLineSegment(sketch, "E43", {"start": v(-3368.67, 152.4) * mm, "end": v(-1988.93, 1828.9) * mm});
            skLineSegment(sketch, "E44", {"start": v(-1988.93, 1828.9) * mm, "end": v(-1981.2, 2133.6) * mm});
            skSolve(sketch);
        }
        {
            var Q0;
            Q0 = qSketchRegion(id + "F62", true);
            extrude(context, id + "F63", {"entities" : qUnion([Q0]), "depth" : 762 * mm, "offsetDistance" : 25.4 * mm});
        }
        {
            var Q0;
            Q0=makeQuery(id+"F57.boolean.opBoolean","COPY",FACE,{"derivedFrom":makeQuery(id+"F57.opExtrude","CAP_FACE",FACE,{"disambiguationData":[OSD([sQuery(id+"F56.wireOp",EDGE,"E38.bottom"),sQuery(id+"F56.wireOp",EDGE,"E38.top"),sQuery(id+"F56.wireOp",EDGE,"E38.left"),sQuery(id+"F56.wireOp",EDGE,"E38.right")])],"isStart":false})});
            var sketch = newSketch(context, id + "F64", { "sketchPlane" : qUnion([Q0])});
            skLineSegment(sketch, "E45.bottom", {"start": v(8991.6, 3810) * mm, "end": v(8229.6, 3810) * mm});
            skLineSegment(sketch, "E45.top", {"start": v(8991.6, 3505.2) * mm, "end": v(8229.6, 3505.2) * mm});
            skLineSegment(sketch, "E45.left", {"start": v(8991.6, 3810) * mm, "end": v(8991.6, 3505.2) * mm});
            skLineSegment(sketch, "E45.right", {"start": v(8229.6, 3810) * mm, "end": v(8229.6, 3505.2) * mm});
            skSolve(sketch);
        }
        {
            var Q0;
            Q0 = qSketchRegion(id + "F64", true);
            extrude(context, id + "F65", {"entities" : qUnion([Q0]), "operationType" : NewBodyOperationType.ADD, "depth" : 3048 * mm, "offsetDistance" : 25.4 * mm});
        }
        {
            var Q0;
            Q0=makeQuery(id+"F57.boolean.opBoolean","COPY",FACE,{"derivedFrom":makeQuery(id+"F57.opExtrude","SWEPT_FACE",FACE,{"disambiguationData":[OSD([sQuery(id+"F56.wireOp",EDGE,"E38.right")])]})});
            var sketch = newSketch(context, id + "F66", { "sketchPlane" : qUnion([Q0])});
            skLineSegment(sketch, "E46", {"start": v(-4804.81, 3810) * mm, "end": v(-4804.81, 3505.2) * mm});
            skPoint(sketch, "E46.endSnap0", {"position": v(-4648.2, 3505.2) * mm});
            skLineSegment(sketch, "E47", {"start": v(-4804.81, 3505.2) * mm, "end": v(-1981.2, 1828.8) * mm});
            skLineSegment(sketch, "E48", {"start": v(-1981.2, 1828.8) * mm, "end": v(-1981.2, 2133.6) * mm});
            skLineSegment(sketch, "E49", {"start": v(-1981.2, 2133.6) * mm, "end": v(-4804.81, 3810) * mm});
            skSolve(sketch);
        }
        {
            var Q0;
            Q0 = qSketchRegion(id + "F66", true);
            extrude(context, id + "F67", {"entities" : qUnion([Q0]), "depth" : 762 * mm, "offsetDistance" : 25.4 * mm});
        }
        {
            var Q0;
            Q0=makeQuery(id+"F67.opExtrude","SWEPT_FACE",FACE,{"disambiguationData":[OSD([sQuery(id+"F66.wireOp",EDGE,"E46")])]});
            var sketch = newSketch(context, id + "F68", { "sketchPlane" : qUnion([Q0])});
            skLineSegment(sketch, "E50.bottom", {"start": v(7467.6, 3810) * mm, "end": v(8229.6, 3810) * mm});
            skLineSegment(sketch, "E50.top", {"start": v(7467.6, 3505.2) * mm, "end": v(8229.6, 3505.2) * mm});
            skLineSegment(sketch, "E50.left", {"start": v(7467.6, 3810) * mm, "end": v(7467.6, 3505.2) * mm});
            skLineSegment(sketch, "E50.right", {"start": v(8229.6, 3810) * mm, "end": v(8229.6, 3505.2) * mm});
            skSolve(sketch);
        }
        {
            var Q0;
            Q0 = qSketchRegion(id + "F68", true);
            extrude(context, id + "F69", {"entities" : qUnion([Q0]), "depth" : 1371.6 * mm, "offsetDistance" : 25.4 * mm});
        }
        {
            var Q0;
            Q0=makeQuery(id+"F65.boolean.opBoolean","MERGE",FACE,{"derivedFrom":[makeQuery(id+"F38.opExtrude","CAP_FACE",FACE,{"disambiguationData":[OSD([sQuery(id+"F37.wireOp",EDGE,"E23.bottom"),sQuery(id+"F37.wireOp",EDGE,"E23.top"),sQuery(id+"F37.wireOp",EDGE,"E23.left"),sQuery(id+"F37.wireOp",EDGE,"E23.right")])],"isStart":false}),makeQuery(id+"F65.opExtrude","SWEPT_FACE",FACE,{"disambiguationData":[OSD([sQuery(id+"F64.wireOp",EDGE,"E45.bottom")])]})]});
            var sketch = newSketch(context, id + "F70", { "sketchPlane" : qUnion([Q0])});
            skLineSegment(sketch, "E51.bottom", {"start": v(6172.2, 8991.6) * mm, "end": v(3124.2, 8991.6) * mm});
            skLineSegment(sketch, "E51.top", {"start": v(6172.2, 8229.6) * mm, "end": v(3124.2, 8229.6) * mm});
            skLineSegment(sketch, "E51.left", {"start": v(6172.2, 8991.6) * mm, "end": v(6172.2, 8229.6) * mm});
            skLineSegment(sketch, "E51.right", {"start": v(3124.2, 8991.6) * mm, "end": v(3124.2, 8229.6) * mm});
            skSolve(sketch);
        }
        {
            var Q0;
            Q0 = qSketchRegion(id + "F70", true);
            extrude(context, id + "F71", {"entities" : qUnion([Q0]), "operationType" : NewBodyOperationType.REMOVE, "oppositeDirection" : true, "depth" : 304.8 * mm, "offsetDistance" : 25.4 * mm});
        }
    });
